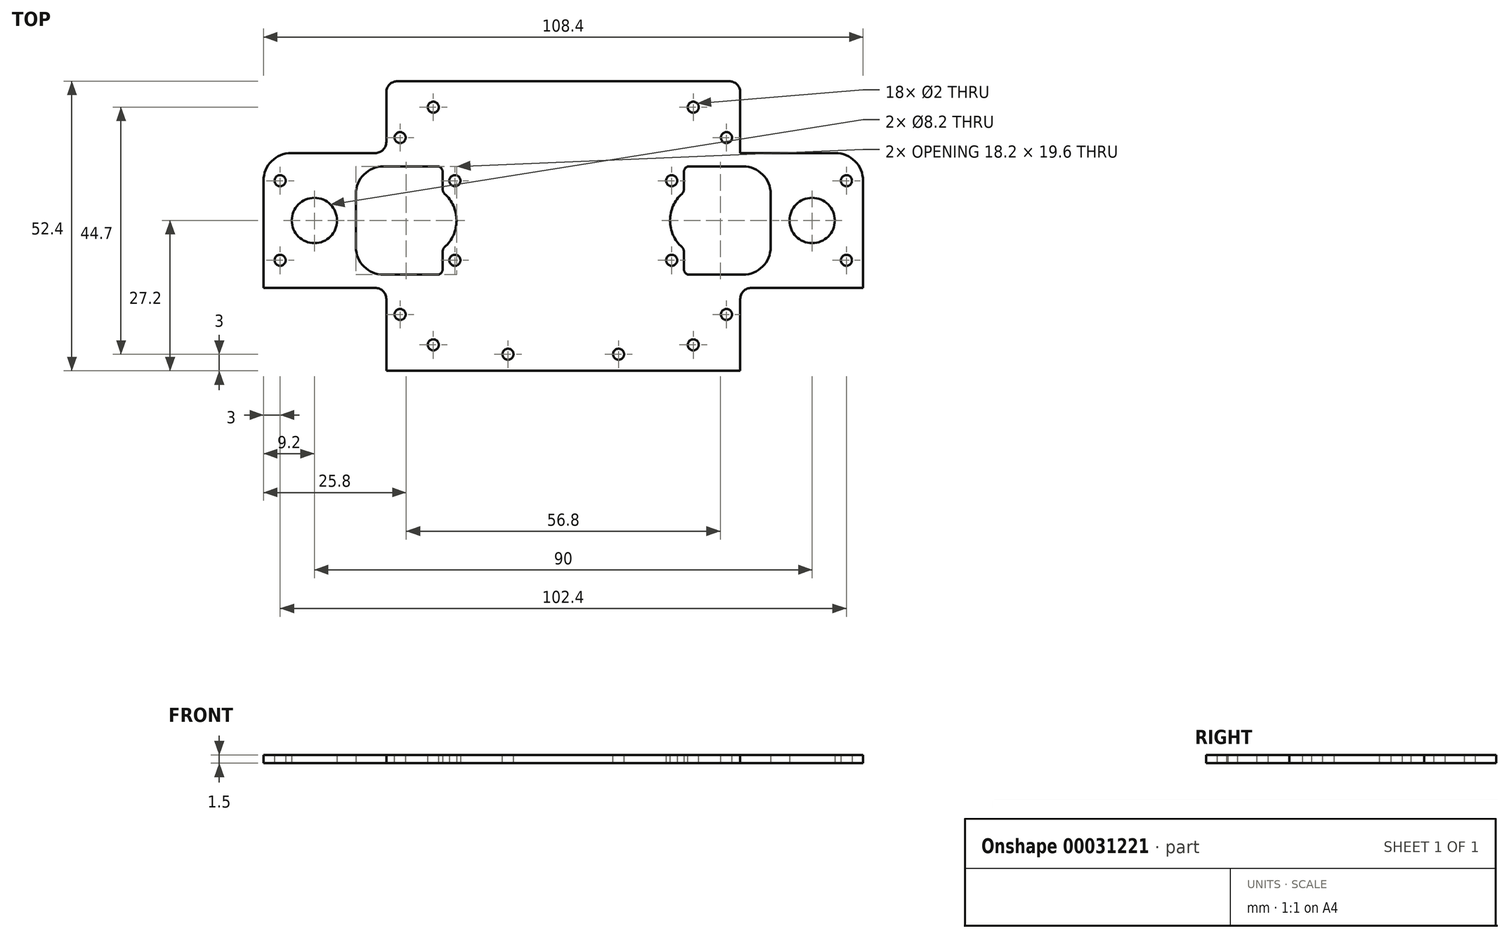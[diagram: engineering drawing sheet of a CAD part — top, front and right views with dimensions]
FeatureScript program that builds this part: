
annotation { "Feature Type Name" : "Feature", "Feature Type Description" : "" }
export const myFeature = defineFeature(function(context is Context, id is Id, definition is map)
    precondition{}
    {
        {
            var Q0;
            Q0=qCreatedBy(makeId("Top.planeOp"),FACE);
            var sketch = newSketch(context, id + "F0", { "sketchPlane" : qUnion([Q0])});
            skLineSegment(sketch, "E0.bottom", {"start": v(54.2, -12.2) * mm, "end": v(-54.2, -12.2) * mm});
            skLineSegment(sketch, "E0.top", {"start": v(54.2, 12.2) * mm, "end": v(-54.2, 12.2) * mm});
            skLineSegment(sketch, "E0.left", {"start": v(54.2, -12.2) * mm, "end": v(54.2, 12.2) * mm});
            skLineSegment(sketch, "E0.right", {"start": v(-54.2, -12.2) * mm, "end": v(-54.2, 12.2) * mm});
            skPoint(sketch, "E0.middle", {"position": v(0, 0) * mm});
            skCircle(sketch, "E1", {"center": v(-45, 0) * mm, "radius": 4.1 * mm});
            skCircle(sketch, "E2", {"center": v(-51.2, 7.2) * mm, "radius": 1 * mm});
            skCircle(sketch, "E3", {"center": v(-19.6, 7.2) * mm, "radius": 1 * mm});
            skLineSegment(sketch, "E4.bottom", {"start": v(-32.5, 9.8) * mm, "end": v(-22.8, 9.8) * mm});
            skLineSegment(sketch, "E4.top", {"start": v(-32.5, -9.8) * mm, "end": v(-22.8, -9.8) * mm});
            skLineSegment(sketch, "E4.left", {"start": v(-37.5, 4.8) * mm, "end": v(-37.5, -4.8) * mm});
            skLineSegment(sketch, "E4.right", {"start": v(-21.8, 8.8) * mm, "end": v(-21.8, 5.6) * mm});
            skPoint(sketch, "E4.middle", {"position": v(-29.65, 0) * mm});
            skPoint(sketch, "E5.visualSharp", {"position": v(-37.5, 9.8) * mm});
            skArc(sketch, "E5.filletArc", {"start": v(-32.5, 9.8) * mm, "mid": v(-36.04, 8.34) * mm, "end": v(-37.5, 4.8) * mm});
            skPoint(sketch, "E6.visualSharp", {"position": v(-37.5, -9.8) * mm});
            skArc(sketch, "E6.filletArc", {"start": v(-37.5, -4.8) * mm, "mid": v(-36.04, -8.34) * mm, "end": v(-32.5, -9.8) * mm});
            skPoint(sketch, "E7.visualSharp", {"position": v(-21.8, 9.8) * mm});
            skArc(sketch, "E7.filletArc", {"start": v(-21.8, 8.8) * mm, "mid": v(-22.1, 9.5) * mm, "end": v(-22.8, 9.8) * mm});
            skPoint(sketch, "E8.visualSharp", {"position": v(-21.8, -9.8) * mm});
            skArc(sketch, "E8.filletArc", {"start": v(-22.8, -9.8) * mm, "mid": v(-22.1, -9.5) * mm, "end": v(-21.8, -8.8) * mm});
            skCircle(sketch, "E9.MirrorC", {"center": v(-51.2, -7.2) * mm, "radius": 1 * mm});
            skCircle(sketch, "E10.MirrorC", {"center": v(-19.6, -7.2) * mm, "radius": 1 * mm});
            skArc(sketch, "E11.MirrorCS", {"start": v(21.8, 8.8) * mm, "mid": v(22.1, 9.5) * mm, "end": v(22.8, 9.8) * mm});
            skArc(sketch, "E12.MirrorCS", {"start": v(22.8, -9.8) * mm, "mid": v(22.1, -9.5) * mm, "end": v(21.8, -8.8) * mm});
            skCircle(sketch, "E13.MirrorC", {"center": v(19.6, -7.2) * mm, "radius": 1 * mm});
            skArc(sketch, "E14.MirrorCS", {"start": v(37.5, -4.8) * mm, "mid": v(36.04, -8.34) * mm, "end": v(32.5, -9.8) * mm});
            skArc(sketch, "E15.MirrorCS", {"start": v(32.5, 9.8) * mm, "mid": v(36.04, 8.34) * mm, "end": v(37.5, 4.8) * mm});
            skLineSegment(sketch, "E16.MirrorCS", {"start": v(21.8, 8.8) * mm, "end": v(21.8, 5.6) * mm});
            skPoint(sketch, "E17.MirrorP", {"position": v(21.8, -9.8) * mm});
            skLineSegment(sketch, "E18.MirrorCS", {"start": v(32.5, 9.8) * mm, "end": v(22.8, 9.8) * mm});
            skCircle(sketch, "E19.MirrorC", {"center": v(19.6, 7.2) * mm, "radius": 1 * mm});
            skPoint(sketch, "E20.MirrorP", {"position": v(21.8, 9.8) * mm});
            skPoint(sketch, "E21.MirrorP", {"position": v(29.65, 0) * mm});
            skCircle(sketch, "E22.MirrorC", {"center": v(51.2, -7.2) * mm, "radius": 1 * mm});
            skCircle(sketch, "E23.MirrorC", {"center": v(51.2, 7.2) * mm, "radius": 1 * mm});
            skCircle(sketch, "E24.MirrorC", {"center": v(45, 0) * mm, "radius": 4.1 * mm});
            skLineSegment(sketch, "E25.MirrorCS", {"start": v(37.5, 4.8) * mm, "end": v(37.5, -4.8) * mm});
            skPoint(sketch, "E26.MirrorP", {"position": v(37.5, -9.8) * mm});
            skLineSegment(sketch, "E27.MirrorCS", {"start": v(32.5, -9.8) * mm, "end": v(22.8, -9.8) * mm});
            skPoint(sketch, "E28.MirrorP", {"position": v(37.5, 9.8) * mm});
            skArc(sketch, "E29", {"start": v(-21.47, -4.84) * mm, "mid": v(-19.3, 0) * mm, "end": v(-21.47, 4.84) * mm});
            skLineSegment(sketch, "E30.trimOffspring", {"start": v(-21.8, -5.6) * mm, "end": v(-21.8, -8.8) * mm});
            skPoint(sketch, "E31.visualSharp", {"position": v(-21.8, 5.12) * mm});
            skArc(sketch, "E31.filletArc", {"start": v(-21.8, 5.6) * mm, "mid": v(-21.71, 5.18) * mm, "end": v(-21.47, 4.84) * mm});
            skPoint(sketch, "E32.visualSharp", {"position": v(-21.8, -5.12) * mm});
            skArc(sketch, "E32.filletArc", {"start": v(-21.47, -4.84) * mm, "mid": v(-21.71, -5.18) * mm, "end": v(-21.8, -5.6) * mm});
            skArc(sketch, "E33.MirrorCS", {"start": v(21.8, 5.6) * mm, "mid": v(21.71, 5.18) * mm, "end": v(21.47, 4.84) * mm});
            skArc(sketch, "E34.MirrorCS", {"start": v(21.47, -4.84) * mm, "mid": v(19.3, 0) * mm, "end": v(21.47, 4.84) * mm});
            skPoint(sketch, "E35.MirrorP", {"position": v(21.8, 5.12) * mm});
            skPoint(sketch, "E36.MirrorP", {"position": v(21.8, -5.12) * mm});
            skArc(sketch, "E37.MirrorCS", {"start": v(21.47, -4.84) * mm, "mid": v(21.71, -5.18) * mm, "end": v(21.8, -5.6) * mm});
            skLineSegment(sketch, "E38.trimOffspring", {"start": v(21.8, -5.6) * mm, "end": v(21.8, -8.8) * mm});
            skSolve(sketch);
        }
        {
            var Q0;
            Q0=qSketchRegion(id+"F0",true);
            extrude(context, id + "F1", {"entities" : qUnion([Q0]), "depth" : 1.5 * mm});
        }
        {
            var Q0;
            Q0=makeQuery(id+"F1.opExtrude","SWEPT_FACE",FACE,{"disambiguationData":[OSD([sQuery(id+"F0.wireOp",EDGE,"E0.bottom")])]});
            var sketch = newSketch(context, id + "F2", { "sketchPlane" : qUnion([Q0])});
            skLineSegment(sketch, "E39.bottom", {"start": v(-54.2, 1.5) * mm, "end": v(54.2, 1.5) * mm});
            skLineSegment(sketch, "E39.top", {"start": v(-54.2, 0) * mm, "end": v(54.2, 0) * mm});
            skLineSegment(sketch, "E39.left", {"start": v(-54.2, 1.5) * mm, "end": v(-54.2, 0) * mm});
            skLineSegment(sketch, "E39.right", {"start": v(54.2, 1.5) * mm, "end": v(54.2, 0) * mm});
            skSolve(sketch);
        }
        {
            var Q0;
            Q0 = qSketchRegion(id + "F2", true);
            extrude(context, id + "F3", {"entities" : qUnion([Q0]), "operationType" : NewBodyOperationType.ADD, "depth" : 15 * mm});
        }
        {
            var Q0;
            Q0=makeQuery(id+"F3.boolean.opBoolean","MERGE",FACE,{"derivedFrom":[makeQuery(id+"F1.opExtrude","CAP_FACE",FACE,{"disambiguationData":[OSD([sQuery(id+"F0.wireOp",EDGE,"E0.bottom"),sQuery(id+"F0.wireOp",EDGE,"E0.top"),sQuery(id+"F0.wireOp",EDGE,"E0.left"),sQuery(id+"F0.wireOp",EDGE,"E0.right"),sQuery(id+"F0.wireOp",EDGE,"E1"),sQuery(id+"F0.wireOp",EDGE,"E2"),sQuery(id+"F0.wireOp",EDGE,"E3"),sQuery(id+"F0.wireOp",EDGE,"E4.bottom"),sQuery(id+"F0.wireOp",EDGE,"E4.top"),sQuery(id+"F0.wireOp",EDGE,"E4.left"),sQuery(id+"F0.wireOp",EDGE,"E4.right"),sQuery(id+"F0.wireOp",EDGE,"E5.filletArc"),sQuery(id+"F0.wireOp",EDGE,"E6.filletArc"),sQuery(id+"F0.wireOp",EDGE,"E7.filletArc"),sQuery(id+"F0.wireOp",EDGE,"E8.filletArc"),sQuery(id+"F0.wireOp",EDGE,"E9.MirrorC"),sQuery(id+"F0.wireOp",EDGE,"E10.MirrorC"),sQuery(id+"F0.wireOp",EDGE,"E11.MirrorCS"),sQuery(id+"F0.wireOp",EDGE,"E12.MirrorCS"),sQuery(id+"F0.wireOp",EDGE,"E13.MirrorC"),sQuery(id+"F0.wireOp",EDGE,"E14.MirrorCS"),sQuery(id+"F0.wireOp",EDGE,"E15.MirrorCS"),sQuery(id+"F0.wireOp",EDGE,"E16.MirrorCS"),sQuery(id+"F0.wireOp",EDGE,"E18.MirrorCS"),sQuery(id+"F0.wireOp",EDGE,"E19.MirrorC"),sQuery(id+"F0.wireOp",EDGE,"E22.MirrorC"),sQuery(id+"F0.wireOp",EDGE,"E23.MirrorC"),sQuery(id+"F0.wireOp",EDGE,"E24.MirrorC"),sQuery(id+"F0.wireOp",EDGE,"E25.MirrorCS"),sQuery(id+"F0.wireOp",EDGE,"E27.MirrorCS"),sQuery(id+"F0.wireOp",EDGE,"E29"),sQuery(id+"F0.wireOp",EDGE,"E30.trimOffspring"),sQuery(id+"F0.wireOp",EDGE,"E31.filletArc"),sQuery(id+"F0.wireOp",EDGE,"E32.filletArc"),sQuery(id+"F0.wireOp",EDGE,"E33.MirrorCS"),sQuery(id+"F0.wireOp",EDGE,"E34.MirrorCS"),sQuery(id+"F0.wireOp",EDGE,"E37.MirrorCS"),sQuery(id+"F0.wireOp",EDGE,"E38.trimOffspring")])],"isStart":false}),makeQuery(id+"F3.opExtrude","SWEPT_FACE",FACE,{"disambiguationData":[OSD([sQuery(id+"F2.wireOp",EDGE,"E39.bottom")])]})]});
            var sketch = newSketch(context, id + "F4", { "sketchPlane" : qUnion([Q0])});
            skLineSegment(sketch, "E40.bottom", {"start": v(-54.2, -27.2) * mm, "end": v(-32, -27.2) * mm});
            skLineSegment(sketch, "E40.top", {"start": v(-54.2, -12.2) * mm, "end": v(-32, -12.2) * mm});
            skLineSegment(sketch, "E40.left", {"start": v(-54.2, -27.2) * mm, "end": v(-54.2, -12.2) * mm});
            skLineSegment(sketch, "E40.right", {"start": v(-32, -27.2) * mm, "end": v(-32, -12.2) * mm});
            skPoint(sketch, "E41", {"position": v(-19.6, -7.2) * mm});
            skLineSegment(sketch, "E42.MirrorCS", {"start": v(54.2, -27.2) * mm, "end": v(32, -27.2) * mm});
            skLineSegment(sketch, "E43.MirrorCS", {"start": v(54.2, -12.2) * mm, "end": v(32, -12.2) * mm});
            skLineSegment(sketch, "E44.MirrorCS", {"start": v(54.2, -27.2) * mm, "end": v(54.2, -12.2) * mm});
            skLineSegment(sketch, "E45.MirrorCS", {"start": v(32, -27.2) * mm, "end": v(32, -12.2) * mm});
            skSolve(sketch);
        }
        {
            var Q0;
            Q0 = qSketchRegion(id + "F4", true);
            extrude(context, id + "F5", {"entities" : qUnion([Q0]), "operationType" : NewBodyOperationType.REMOVE, "endBound" : BoundingType.UP_TO_NEXT, "oppositeDirection" : true, "depth" : 25 * mm});
        }
        {
            var Q0;
            Q0=makeQuery(id+"F3.boolean.opBoolean","MERGE",FACE,{"derivedFrom":[makeQuery(id+"F1.opExtrude","CAP_FACE",FACE,{"disambiguationData":[OSD([sQuery(id+"F0.wireOp",EDGE,"E0.bottom"),sQuery(id+"F0.wireOp",EDGE,"E0.top"),sQuery(id+"F0.wireOp",EDGE,"E0.left"),sQuery(id+"F0.wireOp",EDGE,"E0.right"),sQuery(id+"F0.wireOp",EDGE,"E1"),sQuery(id+"F0.wireOp",EDGE,"E2"),sQuery(id+"F0.wireOp",EDGE,"E3"),sQuery(id+"F0.wireOp",EDGE,"E4.bottom"),sQuery(id+"F0.wireOp",EDGE,"E4.top"),sQuery(id+"F0.wireOp",EDGE,"E4.left"),sQuery(id+"F0.wireOp",EDGE,"E4.right"),sQuery(id+"F0.wireOp",EDGE,"E5.filletArc"),sQuery(id+"F0.wireOp",EDGE,"E6.filletArc"),sQuery(id+"F0.wireOp",EDGE,"E7.filletArc"),sQuery(id+"F0.wireOp",EDGE,"E8.filletArc"),sQuery(id+"F0.wireOp",EDGE,"E9.MirrorC"),sQuery(id+"F0.wireOp",EDGE,"E10.MirrorC"),sQuery(id+"F0.wireOp",EDGE,"E11.MirrorCS"),sQuery(id+"F0.wireOp",EDGE,"E12.MirrorCS"),sQuery(id+"F0.wireOp",EDGE,"E13.MirrorC"),sQuery(id+"F0.wireOp",EDGE,"E14.MirrorCS"),sQuery(id+"F0.wireOp",EDGE,"E15.MirrorCS"),sQuery(id+"F0.wireOp",EDGE,"E16.MirrorCS"),sQuery(id+"F0.wireOp",EDGE,"E18.MirrorCS"),sQuery(id+"F0.wireOp",EDGE,"E19.MirrorC"),sQuery(id+"F0.wireOp",EDGE,"E22.MirrorC"),sQuery(id+"F0.wireOp",EDGE,"E23.MirrorC"),sQuery(id+"F0.wireOp",EDGE,"E24.MirrorC"),sQuery(id+"F0.wireOp",EDGE,"E25.MirrorCS"),sQuery(id+"F0.wireOp",EDGE,"E27.MirrorCS"),sQuery(id+"F0.wireOp",EDGE,"E29"),sQuery(id+"F0.wireOp",EDGE,"E30.trimOffspring"),sQuery(id+"F0.wireOp",EDGE,"E31.filletArc"),sQuery(id+"F0.wireOp",EDGE,"E32.filletArc"),sQuery(id+"F0.wireOp",EDGE,"E33.MirrorCS"),sQuery(id+"F0.wireOp",EDGE,"E34.MirrorCS"),sQuery(id+"F0.wireOp",EDGE,"E37.MirrorCS"),sQuery(id+"F0.wireOp",EDGE,"E38.trimOffspring")])],"isStart":false}),makeQuery(id+"F3.opExtrude","SWEPT_FACE",FACE,{"disambiguationData":[OSD([sQuery(id+"F2.wireOp",EDGE,"E39.bottom")])]})]});
            var sketch = newSketch(context, id + "F6", { "sketchPlane" : qUnion([Q0])});
            skLineSegment(sketch, "E46.bottom", {"start": v(-32, -27.2) * mm, "end": v(32, -27.2) * mm, "construction": true});
            skLineSegment(sketch, "E46.top", {"start": v(-32, 12.2) * mm, "end": v(32, 12.2) * mm, "construction": true});
            skLineSegment(sketch, "E46.left", {"start": v(-32, -27.2) * mm, "end": v(-32, 12.2) * mm, "construction": true});
            skLineSegment(sketch, "E46.right", {"start": v(32, -27.2) * mm, "end": v(32, 12.2) * mm, "construction": true});
            skLineSegment(sketch, "E47", {"start": v(-32, -12.2) * mm, "end": v(32, -12.2) * mm, "construction": true});
            skCircle(sketch, "E48", {"center": v(-23.5, -33.7) * mm, "radius": 1 * mm, "construction": true});
            skCircle(sketch, "E49.MirrorC", {"center": v(-23.5, 9.3) * mm, "radius": 1 * mm, "construction": true});
            skCircle(sketch, "E50.MirrorC", {"center": v(23.5, 9.3) * mm, "radius": 1 * mm, "construction": true});
            skCircle(sketch, "E51.MirrorC", {"center": v(23.5, -33.7) * mm, "radius": 1 * mm, "construction": true});
            skCircle(sketch, "E52", {"center": v(-10, -24.2) * mm, "radius": 1 * mm});
            skCircle(sketch, "E53.MirrorC", {"center": v(10, -24.2) * mm, "radius": 1 * mm});
            skSolve(sketch);
        }
        {
            var Q0;
            Q0=makeQuery(id+"F5.boolean.opBoolean","COPY",EDGE,{"derivedFrom":makeQuery(id+"F5.opExtrude","SWEPT_EDGE",EDGE,{"disambiguationData":[OSD([sQuery(id+"F4.wireOp",EDGE,"E40.top"),sQuery(id+"F4.wireOp",EDGE,"E40.right")])]})});
            var Q1;
            Q1=makeQuery(id+"F5.boolean.opBoolean","COPY",EDGE,{"derivedFrom":makeQuery(id+"F5.opExtrude","SWEPT_EDGE",EDGE,{"disambiguationData":[OSD([sQuery(id+"F4.wireOp",EDGE,"E43.MirrorCS"),sQuery(id+"F4.wireOp",EDGE,"E45.MirrorCS")])]})});
            fillet(context, id + "F7", {"entities" : qUnion([Q0, Q1]), "radius" : 2 * mm, "tangentPropagation" : true, "allowEdgeOverflow" : false});
        }
        {
            var Q0;
            Q0=makeQuery(id+"F1.opExtrude","SWEPT_EDGE",EDGE,{"disambiguationData":[OSD([sQuery(id+"F0.wireOp",EDGE,"E0.top"),sQuery(id+"F0.wireOp",EDGE,"E0.right")])]});
            var Q1;
            Q1=makeQuery(id+"F5.boolean.opBoolean","COPY",EDGE,{"derivedFrom":makeQuery(id+"F5.opExtrude","SWEPT_EDGE",EDGE,{"disambiguationData":[OSD([sQuery(id+"F0.wireOp",EDGE,"E0.right"),sQuery(id+"F2.wireOp",EDGE,"E39.bottom"),sQuery(id+"F2.wireOp",EDGE,"E39.left"),sQuery(id+"F4.wireOp",EDGE,"E40.top"),sQuery(id+"F4.wireOp",EDGE,"E40.left")])]})});
            var Q2;
            Q2=makeQuery(id+"F1.opExtrude","SWEPT_EDGE",EDGE,{"disambiguationData":[OSD([sQuery(id+"F0.wireOp",EDGE,"E0.top"),sQuery(id+"F0.wireOp",EDGE,"E0.left")])]});
            var Q3;
            Q3=makeQuery(id+"F5.boolean.opBoolean","COPY",EDGE,{"derivedFrom":makeQuery(id+"F5.opExtrude","SWEPT_EDGE",EDGE,{"disambiguationData":[OSD([sQuery(id+"F0.wireOp",EDGE,"E0.left"),sQuery(id+"F2.wireOp",EDGE,"E39.bottom"),sQuery(id+"F2.wireOp",EDGE,"E39.right"),sQuery(id+"F4.wireOp",EDGE,"E43.MirrorCS"),sQuery(id+"F4.wireOp",EDGE,"E44.MirrorCS")])]})});
            fillet(context, id + "F8", {"entities" : qUnion([Q0, Q1, Q2, Q3]), "radius" : 5 * mm, "tangentPropagation" : true, "allowEdgeOverflow" : false});
        }
        {
            var Q0;
            Q0=makeQuery(id+"F1.opExtrude","SWEPT_FACE",FACE,{"disambiguationData":[OSD([sQuery(id+"F0.wireOp",EDGE,"E0.top")])]});
            var sketch = newSketch(context, id + "F9", { "sketchPlane" : qUnion([Q0])});
            skLineSegment(sketch, "E54.bottom", {"start": v(0, 0) * mm, "end": v(-32, 0) * mm});
            skLineSegment(sketch, "E54.top", {"start": v(0, 1.5) * mm, "end": v(-32, 1.5) * mm});
            skLineSegment(sketch, "E54.left", {"start": v(0, 0) * mm, "end": v(0, 1.5) * mm});
            skLineSegment(sketch, "E54.right", {"start": v(-32, 0) * mm, "end": v(-32, 1.5) * mm});
            skLineSegment(sketch, "E55.MirrorCS", {"start": v(32, 0) * mm, "end": v(32, 1.5) * mm});
            skLineSegment(sketch, "E56.MirrorCS", {"start": v(0, 0) * mm, "end": v(32, 0) * mm});
            skLineSegment(sketch, "E57.MirrorCS", {"start": v(0, 1.5) * mm, "end": v(32, 1.5) * mm});
            skSolve(sketch);
        }
        {
            var Q0;
            Q0 = qSketchRegion(id + "F9", true);
            extrude(context, id + "F10", {"entities" : qUnion([Q0]), "operationType" : NewBodyOperationType.ADD, "depth" : 13 * mm});
        }
        {
            var Q0;
            Q0 = qSketchRegion(id + "F6", true);
            extrude(context, id + "F11", {"entities" : qUnion([Q0]), "operationType" : NewBodyOperationType.REMOVE, "endBound" : BoundingType.UP_TO_NEXT, "oppositeDirection" : true, "depth" : 25 * mm});
        }
        {
            var Q0;
            Q0=makeQuery(id+"F10.boolean.opBoolean","MERGE",FACE,{"derivedFrom":[makeQuery(id+"F3.boolean.opBoolean","MERGE",FACE,{"derivedFrom":[makeQuery(id+"F1.opExtrude","CAP_FACE",FACE,{"disambiguationData":[OSD([sQuery(id+"F0.wireOp",EDGE,"E0.bottom"),sQuery(id+"F0.wireOp",EDGE,"E0.top"),sQuery(id+"F0.wireOp",EDGE,"E0.left"),sQuery(id+"F0.wireOp",EDGE,"E0.right"),sQuery(id+"F0.wireOp",EDGE,"E1"),sQuery(id+"F0.wireOp",EDGE,"E2"),sQuery(id+"F0.wireOp",EDGE,"E3"),sQuery(id+"F0.wireOp",EDGE,"E4.bottom"),sQuery(id+"F0.wireOp",EDGE,"E4.top"),sQuery(id+"F0.wireOp",EDGE,"E4.left"),sQuery(id+"F0.wireOp",EDGE,"E4.right"),sQuery(id+"F0.wireOp",EDGE,"E5.filletArc"),sQuery(id+"F0.wireOp",EDGE,"E6.filletArc"),sQuery(id+"F0.wireOp",EDGE,"E7.filletArc"),sQuery(id+"F0.wireOp",EDGE,"E8.filletArc"),sQuery(id+"F0.wireOp",EDGE,"E9.MirrorC"),sQuery(id+"F0.wireOp",EDGE,"E10.MirrorC"),sQuery(id+"F0.wireOp",EDGE,"E11.MirrorCS"),sQuery(id+"F0.wireOp",EDGE,"E12.MirrorCS"),sQuery(id+"F0.wireOp",EDGE,"E13.MirrorC"),sQuery(id+"F0.wireOp",EDGE,"E14.MirrorCS"),sQuery(id+"F0.wireOp",EDGE,"E15.MirrorCS"),sQuery(id+"F0.wireOp",EDGE,"E16.MirrorCS"),sQuery(id+"F0.wireOp",EDGE,"E18.MirrorCS"),sQuery(id+"F0.wireOp",EDGE,"E19.MirrorC"),sQuery(id+"F0.wireOp",EDGE,"E22.MirrorC"),sQuery(id+"F0.wireOp",EDGE,"E23.MirrorC"),sQuery(id+"F0.wireOp",EDGE,"E24.MirrorC"),sQuery(id+"F0.wireOp",EDGE,"E25.MirrorCS"),sQuery(id+"F0.wireOp",EDGE,"E27.MirrorCS"),sQuery(id+"F0.wireOp",EDGE,"E29"),sQuery(id+"F0.wireOp",EDGE,"E30.trimOffspring"),sQuery(id+"F0.wireOp",EDGE,"E31.filletArc"),sQuery(id+"F0.wireOp",EDGE,"E32.filletArc"),sQuery(id+"F0.wireOp",EDGE,"E33.MirrorCS"),sQuery(id+"F0.wireOp",EDGE,"E34.MirrorCS"),sQuery(id+"F0.wireOp",EDGE,"E37.MirrorCS"),sQuery(id+"F0.wireOp",EDGE,"E38.trimOffspring")])],"isStart":false}),makeQuery(id+"F3.opExtrude","SWEPT_FACE",FACE,{"disambiguationData":[OSD([sQuery(id+"F2.wireOp",EDGE,"E39.bottom")])]})]}),makeQuery(id+"F10.opExtrude","SWEPT_FACE",FACE,{"disambiguationData":[OSD([sQuery(id+"F9.wireOp",EDGE,"E54.top"),sQuery(id+"F9.wireOp",EDGE,"E57.MirrorCS")])]})]});
            var sketch = newSketch(context, id + "F12", { "sketchPlane" : qUnion([Q0])});
            skLineSegment(sketch, "E58", {"start": v(-32, 25.2) * mm, "end": v(-32, -27.2) * mm, "construction": true});
            skLineSegment(sketch, "E59", {"start": v(32, 25.2) * mm, "end": v(32, -27.2) * mm, "construction": true});
            skLineSegment(sketch, "E60", {"start": v(32, -27.2) * mm, "end": v(31.5, -26.76) * mm, "construction": true});
            skLineSegment(sketch, "E61", {"start": v(-32, -1) * mm, "end": v(32, -1) * mm, "construction": true});
            skCircle(sketch, "E62", {"center": v(-23.5, 20.5) * mm, "radius": 1 * mm});
            skCircle(sketch, "E63.MirrorC", {"center": v(23.5, 20.5) * mm, "radius": 1 * mm});
            skCircle(sketch, "E64.MirrorC", {"center": v(-23.5, -22.5) * mm, "radius": 1 * mm});
            skCircle(sketch, "E65.MirrorC", {"center": v(23.5, -22.5) * mm, "radius": 1 * mm});
            skCircle(sketch, "E66", {"center": v(-29.5, 15) * mm, "radius": 1 * mm});
            skCircle(sketch, "E67.MirrorC", {"center": v(-29.5, -17) * mm, "radius": 1 * mm});
            skCircle(sketch, "E68.MirrorC", {"center": v(29.5, 15) * mm, "radius": 1 * mm});
            skCircle(sketch, "E69.MirrorC", {"center": v(29.5, -17) * mm, "radius": 1 * mm});
            skSolve(sketch);
        }
        {
            var Q0;
            Q0 = qSketchRegion(id + "F12", true);
            extrude(context, id + "F13", {"entities" : qUnion([Q0]), "operationType" : NewBodyOperationType.REMOVE, "endBound" : BoundingType.UP_TO_NEXT, "oppositeDirection" : true, "depth" : 25 * mm});
        }
        {
            var Q0;
            Q0=makeQuery(id+"F5.boolean.opBoolean","COPY",EDGE,{"derivedFrom":makeQuery(id+"F5.opExtrude","SWEPT_EDGE",EDGE,{"disambiguationData":[OSD([sQuery(id+"F2.wireOp",EDGE,"E39.bottom"),sQuery(id+"F4.wireOp",EDGE,"E40.bottom"),sQuery(id+"F4.wireOp",EDGE,"E40.right")])]})});
            var Q1;
            Q1=makeQuery(id+"F5.boolean.opBoolean","COPY",EDGE,{"derivedFrom":makeQuery(id+"F5.opExtrude","SWEPT_EDGE",EDGE,{"disambiguationData":[OSD([sQuery(id+"F2.wireOp",EDGE,"E39.bottom"),sQuery(id+"F4.wireOp",EDGE,"E42.MirrorCS"),sQuery(id+"F4.wireOp",EDGE,"E45.MirrorCS")])]})});
            var Q2;
            Q2=makeQuery(id+"F10.opExtrude","CAP_EDGE",EDGE,{"disambiguationData":[OSD([sQuery(id+"F9.wireOp",EDGE,"E54.right")])],"isStart":false});
            var Q3;
            Q3=makeQuery(id+"F10.opExtrude","CAP_EDGE",EDGE,{"disambiguationData":[OSD([sQuery(id+"F9.wireOp",EDGE,"E54.right")])],"isStart":true});
            var Q4;
            Q4=makeQuery(id+"F10.opExtrude","CAP_EDGE",EDGE,{"disambiguationData":[OSD([sQuery(id+"F9.wireOp",EDGE,"E55.MirrorCS")])],"isStart":true});
            var Q5;
            Q5=makeQuery(id+"F10.opExtrude","CAP_EDGE",EDGE,{"disambiguationData":[OSD([sQuery(id+"F9.wireOp",EDGE,"E55.MirrorCS")])],"isStart":false});
            fillet(context, id + "F14", {"entities" : qUnion([Q0, Q1, Q2, Q3, Q4, Q5]), "radius" : 2 * mm, "tangentPropagation" : true, "allowEdgeOverflow" : false});
        }
    });
